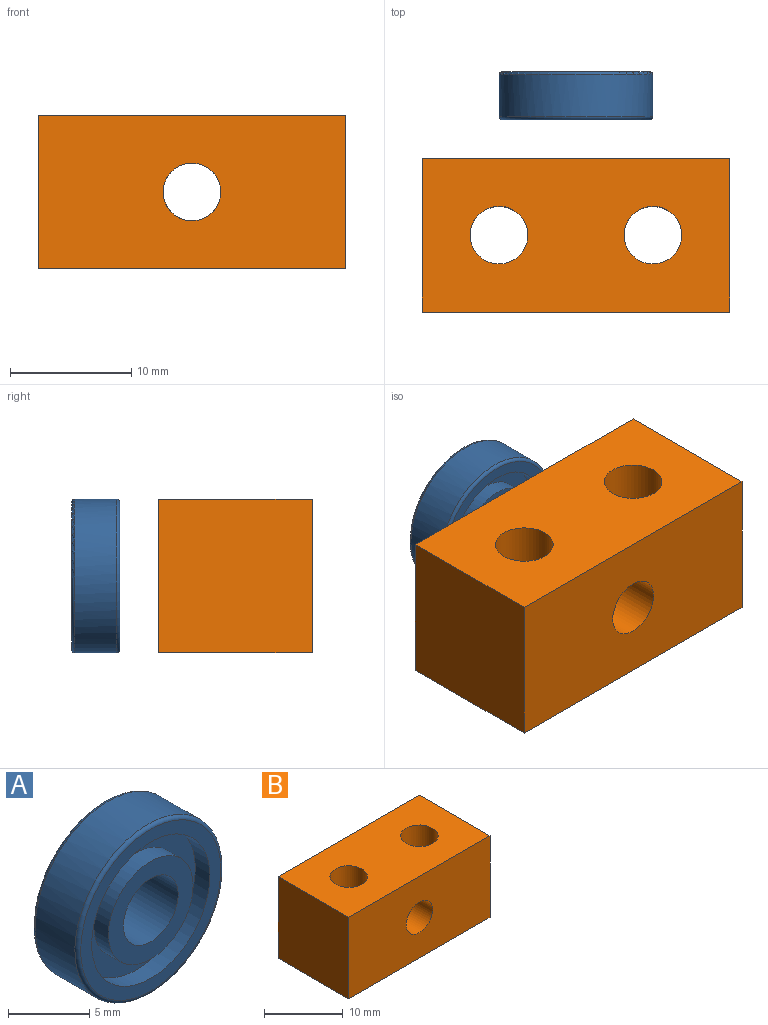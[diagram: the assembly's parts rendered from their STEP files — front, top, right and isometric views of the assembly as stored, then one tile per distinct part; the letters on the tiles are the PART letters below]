
ASSEMBLY  parts=2 mates=2
PART A: 14 faces, bbox 13.7x4x13.7 mm
  f0: torus R=6.1mm, axis (0,1,0), area 15.7mm2, adj f4,f11
  f1: torus R=6.1mm, axis (0,-1,0), area 15.7mm2, adj f4,f12
  f2: cylinder r=3.68mm len=7.37mm, axis (0,-1,0), area 29.4mm2, adj f8,f13
  f3: cylinder r=5.14mm len=10.29mm, axis (0,-1,0), area 41mm2, adj f12,f13
  f4: cylinder r=6.35mm len=12.7mm, axis (0,-1,0), area 137.8mm2, adj f0,f1
  f5: cylinder r=5.14mm len=10.29mm, axis (0,-1,0), area 41mm2, adj f10,f11
  f6: cylinder r=3.68mm len=7.37mm, axis (0,-1,0), area 29.4mm2, adj f9,f10
  f7: cylinder r=2.38mm len=4.76mm, axis (0,-1,0), area 59.3mm2, adj f8,f9
  f8: plane 7.37x7.37mm, normal (0,-1,0), area 24.8mm2, adj f2,f7
  f9: plane 7.37x7.37mm, normal (0,1,0), area 24.8mm2, adj f6,f7
  f10: plane 10.29x10.29mm, normal (0,1,0), area 40.5mm2, adj f5,f6
  f11: plane 12.19x12.19mm, normal (0,1,0), area 33.6mm2, adj f0,f5
  f12: plane 12.19x12.19mm, normal (0,-1,0), area 33.6mm2, adj f1,f3
  f13: plane 10.29x10.29mm, normal (0,-1,0), area 40.5mm2, adj f2,f3
PART B: 9 faces, bbox 25.4x12.7x12.7 mm
  f0: plane 25.4x12.7mm, normal (0,-1,0), area 304.8mm2, adj f1,f5,f6,f7,f8
  f1: plane 12.7x12.7mm, normal (1,0,0), area 161.3mm2, adj f0,f2,f6,f7
  f2: plane 25.4x12.7mm, normal (0,1,0), area 304.8mm2, adj f1,f5,f6,f7,f8
  f3: cylinder r=2.38mm len=12.7mm, axis (0,0,-1), area 190mm2, adj f6,f7
  f4: cylinder r=2.38mm len=12.7mm, axis (0,0,-1), area 190mm2, adj f6,f7
  f5: plane 12.7x12.7mm, normal (-1,0,0), area 161.3mm2, adj f0,f2,f6,f7
  f6: plane 25.4x12.7mm, normal (0,0,1), area 287mm2, adj f0,f1,f2,f3,f4,f5
  f7: plane 25.4x12.7mm, normal (0,0,-1), area 287mm2, adj f0,f1,f2,f3,f4,f5
  f8: cylinder r=2.38mm len=12.7mm, axis (0,-1,0), area 190mm2, adj f0,f2
PLACE A t=(-6.84,-3.28,6.34)mm
PLACE B t=(-6.84,-12.8,-0.01)mm
MATE cylindrical A.f0 <-> B.f8  axis (0,-1,0) through (-6.84,-3.28,6.34)mm
MATE planar A.f0 <-> B.f8  axis (0,-1,0) through (-6.84,-3.28,6.34)mm
